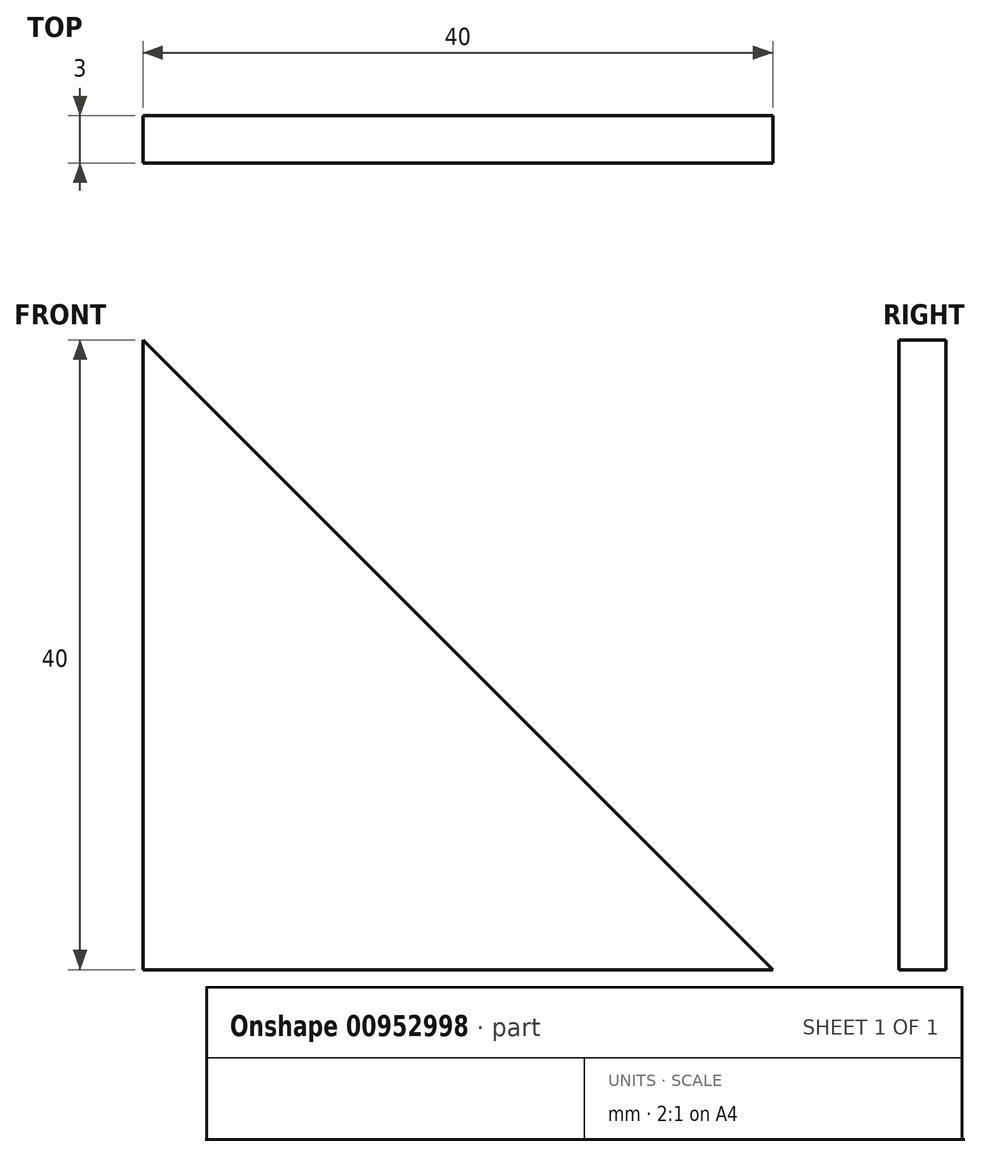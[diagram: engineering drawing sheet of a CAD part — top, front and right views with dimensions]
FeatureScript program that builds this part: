
annotation { "Feature Type Name" : "Feature", "Feature Type Description" : "" }
export const myFeature = defineFeature(function(context is Context, id is Id, definition is map)
    precondition{}
    {
        {
            var Q0;
            Q0=qCreatedBy(makeId("Front.planeOp"),FACE);
            var sketch = newSketch(context, id + "F0", { "sketchPlane" : qUnion([Q0])});
            skLineSegment(sketch, "E0", {"start": v(0, 40) * mm, "end": v(0, 0) * mm});
            skLineSegment(sketch, "E1", {"start": v(0, 0) * mm, "end": v(40, 0) * mm});
            skLineSegment(sketch, "E2", {"start": v(40, 0) * mm, "end": v(0, 40) * mm});
            skSolve(sketch);
        }
        {
            var Q0;
            Q0=makeQuery(id+"F0.imprint","IMPRINT",FACE,{"disambiguationData":[TD([[makeQuery(id+"F0.imprint","IMPRINT",EDGE,{"derivedFrom":sQuery(id+"F0.wireOp",EDGE,"E0")}),1.0]])]});
            extrude(context, id + "F1", {"entities" : qUnion([Q0]), "depth" : 3 * mm, "offsetDistance" : 25 * mm});
        }
    });
